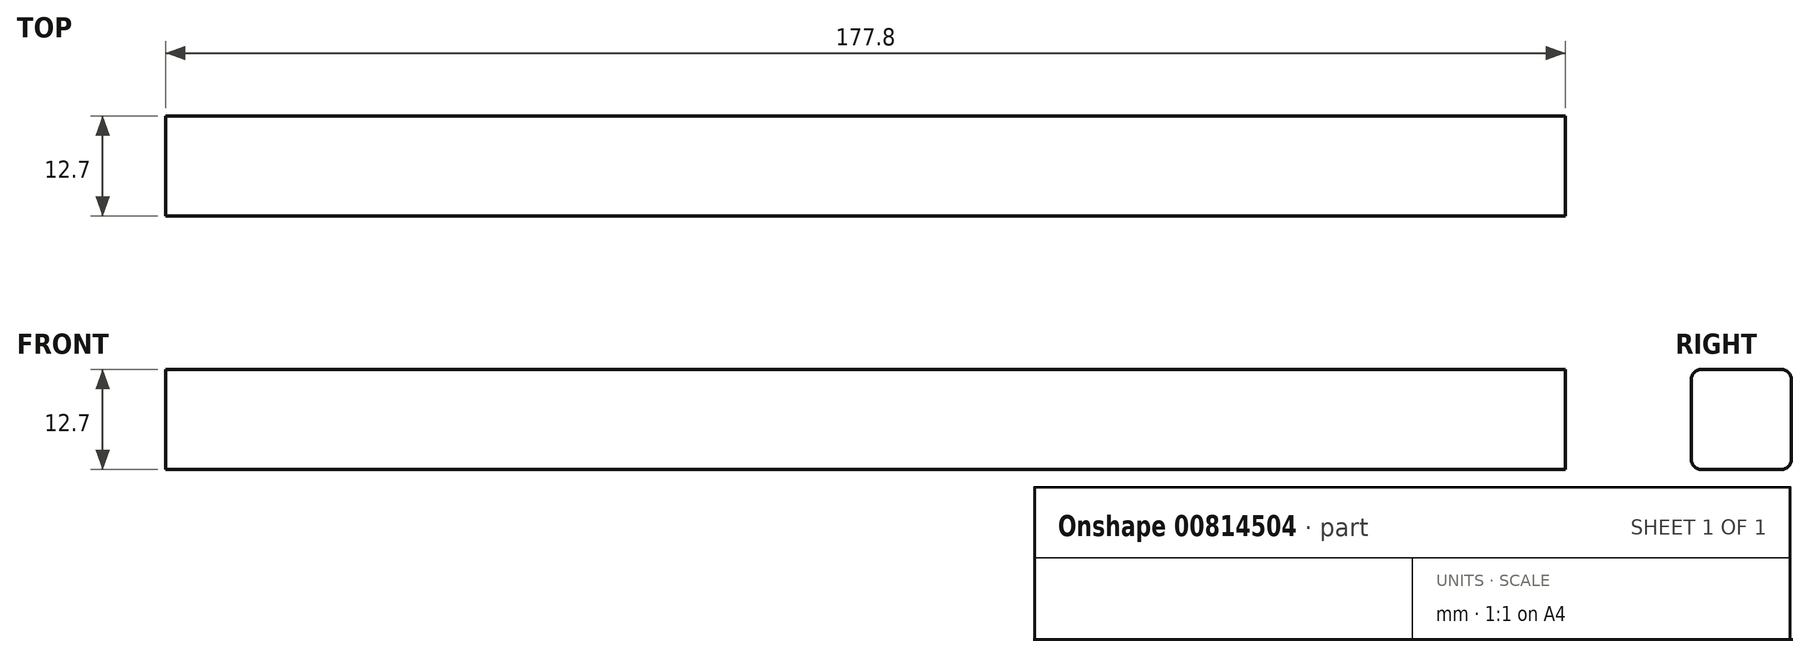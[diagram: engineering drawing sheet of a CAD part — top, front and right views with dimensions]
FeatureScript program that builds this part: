
annotation { "Feature Type Name" : "Feature", "Feature Type Description" : "" }
export const myFeature = defineFeature(function(context is Context, id is Id, definition is map)
    precondition{}
    {
        {
            var Q0;
            Q0=qCreatedBy(makeId("Top.planeOp"),FACE);
            var sketch = newSketch(context, id + "F0", { "sketchPlane" : qUnion([Q0])});
            skLineSegment(sketch, "E0.bottom", {"start": v(88.9, -6.35) * mm, "end": v(-88.9, -6.35) * mm});
            skLineSegment(sketch, "E0.top", {"start": v(88.9, 6.35) * mm, "end": v(-88.9, 6.35) * mm});
            skLineSegment(sketch, "E0.left", {"start": v(88.9, -6.35) * mm, "end": v(88.9, 6.35) * mm});
            skLineSegment(sketch, "E0.right", {"start": v(-88.9, -6.35) * mm, "end": v(-88.9, 6.35) * mm});
            skPoint(sketch, "E0.middle", {"position": v(0, 0) * mm});
            skSolve(sketch);
        }
        {
            var Q0;
            Q0=makeQuery(id+"F0.imprint","IMPRINT",FACE,{"disambiguationData":[TD([[makeQuery(id+"F0.imprint","IMPRINT",EDGE,{"derivedFrom":sQuery(id+"F0.wireOp",EDGE,"E0.bottom")}),-1.0]])]});
            extrude(context, id + "F1", {"entities" : qUnion([Q0]), "depth" : 12.7 * mm, "offsetDistance" : 25.4 * mm});
        }
        {
            var Q0;
            Q0=makeQuery(id+"F1.opExtrude","CAP_EDGE",EDGE,{"disambiguationData":[OSD([sQuery(id+"F0.wireOp",EDGE,"E0.top")])],"isStart":true});
            var Q1;
            Q1=makeQuery(id+"F1.opExtrude","CAP_EDGE",EDGE,{"disambiguationData":[OSD([sQuery(id+"F0.wireOp",EDGE,"E0.top")])],"isStart":false});
            var Q2;
            Q2=makeQuery(id+"F1.opExtrude","CAP_EDGE",EDGE,{"disambiguationData":[OSD([sQuery(id+"F0.wireOp",EDGE,"E0.bottom")])],"isStart":false});
            var Q3;
            Q3=makeQuery(id+"F1.opExtrude","CAP_EDGE",EDGE,{"disambiguationData":[OSD([sQuery(id+"F0.wireOp",EDGE,"E0.bottom")])],"isStart":true});
            fillet(context, id + "F2", {"entities" : qUnion([Q0, Q1, Q2, Q3]), "radius" : 1.27 * mm, "tangentPropagation" : true, "allowEdgeOverflow" : false});
        }
    });
